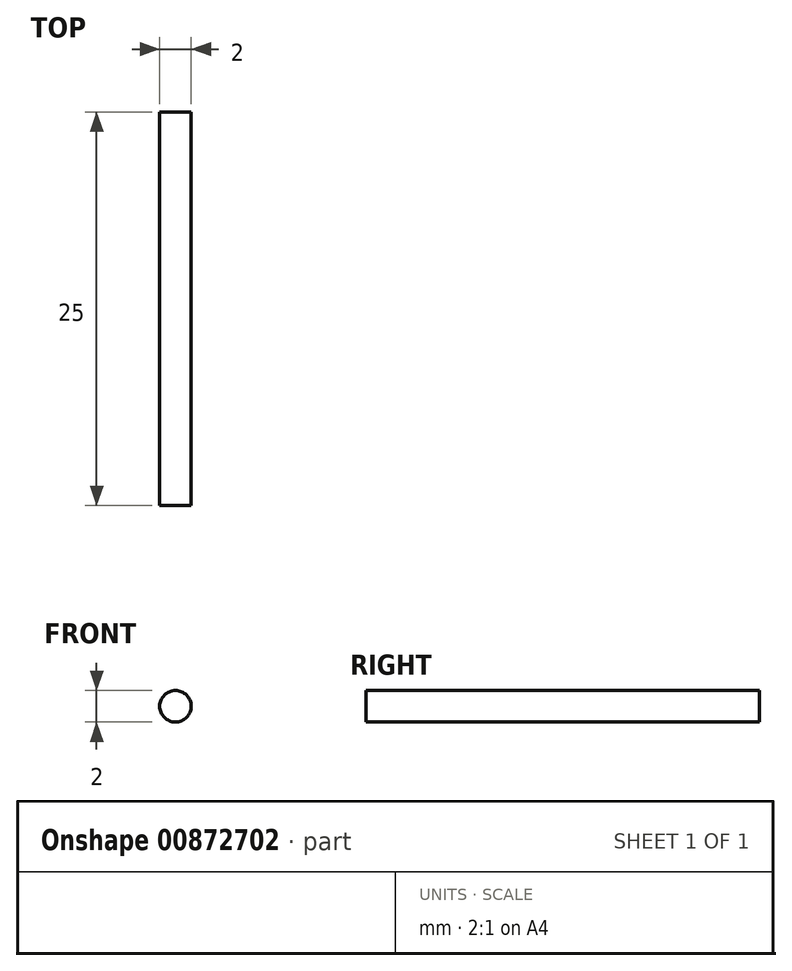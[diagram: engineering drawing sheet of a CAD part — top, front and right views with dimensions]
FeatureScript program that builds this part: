
annotation { "Feature Type Name" : "Feature", "Feature Type Description" : "" }
export const myFeature = defineFeature(function(context is Context, id is Id, definition is map)
    precondition{}
    {
        {
            var Q0;
            Q0=qCreatedBy(makeId("Front.planeOp"),FACE);
            var sketch = newSketch(context, id + "F0", { "sketchPlane" : qUnion([Q0])});
            skCircle(sketch, "E0", {"center": v(0, 0) * mm, "radius": 1 * mm});
            skSolve(sketch);
        }
        {
            var Q0;
            Q0=makeQuery(id+"F0.imprint","IMPRINT",FACE,{"disambiguationData":[TD([[makeQuery(id+"F0.imprint","IMPRINT",EDGE,{"derivedFrom":sQuery(id+"F0.wireOp",EDGE,"E0")}),1.0]])]});
            extrude(context, id + "F1", {"entities" : qUnion([Q0]), "depth" : 25 * mm, "offsetDistance" : 25 * mm});
        }
    });
